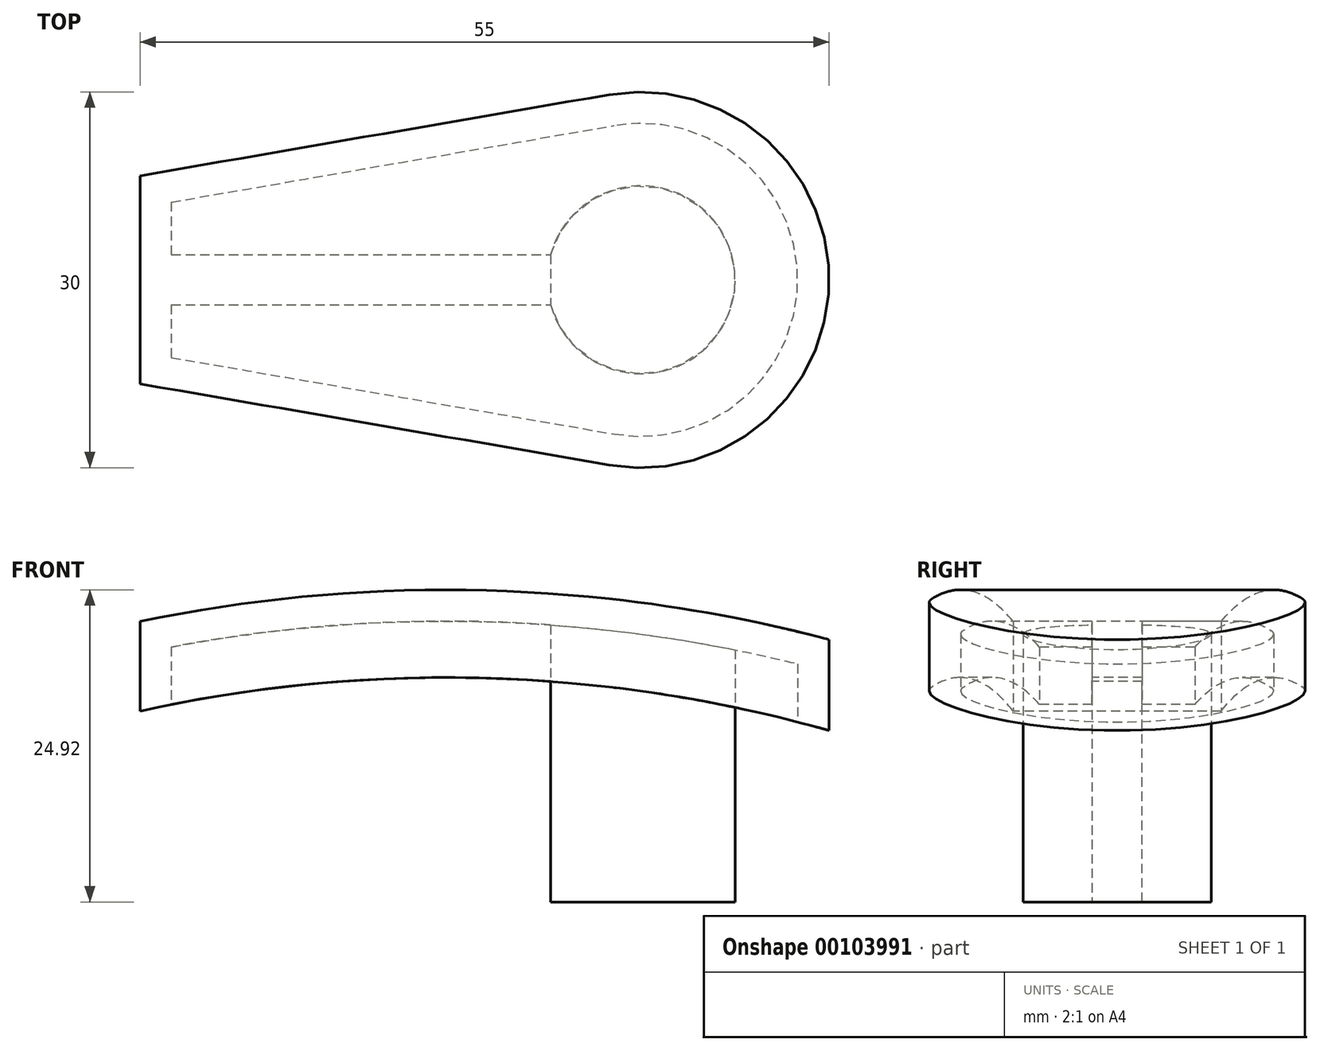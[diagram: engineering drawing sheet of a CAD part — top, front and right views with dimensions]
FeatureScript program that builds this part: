
annotation { "Feature Type Name" : "Feature", "Feature Type Description" : "" }
export const myFeature = defineFeature(function(context is Context, id is Id, definition is map)
    precondition{}
    {
        {
            var Q0;
            Q0=qCreatedBy(makeId("Top.planeOp"),FACE);
            var sketch = newSketch(context, id + "F0", { "sketchPlane" : qUnion([Q0])});
            skArc(sketch, "E0", {"start": v(-2.56, -14.78) * mm, "mid": v(15, 0) * mm, "end": v(-2.56, 14.78) * mm});
            skLineSegment(sketch, "E1", {"start": v(-40, 8.3) * mm, "end": v(-40, 0) * mm});
            skLineSegment(sketch, "E2", {"start": v(-40, 8.3) * mm, "end": v(-2.56, 14.78) * mm});
            skLineSegment(sketch, "E3", {"start": v(0, 0) * mm, "end": v(-66.42, 0) * mm, "construction": true});
            skLineSegment(sketch, "E4.MirrorCS", {"start": v(-40, -8.3) * mm, "end": v(-40, 0) * mm});
            skLineSegment(sketch, "E5.MirrorCS", {"start": v(-40, -8.3) * mm, "end": v(-2.56, -14.78) * mm});
            skSolve(sketch);
        }
        {
            var Q0;
            Q0=makeQuery(id+"F0.imprint","IMPRINT",FACE,{"disambiguationData":[TD([[makeQuery(id+"F0.imprint","IMPRINT",EDGE,{"derivedFrom":sQuery(id+"F0.wireOp",EDGE,"E0")}),1.0]])]});
            extrude(context, id + "F1", {"entities" : qUnion([Q0]), "endBound" : BoundingType.SYMMETRIC, "depth" : 30 * mm});
        }
        {
            var Q0;
            Q0=qCreatedBy(makeId("Front.planeOp"),FACE);
            var sketch = newSketch(context, id + "F2", { "sketchPlane" : qUnion([Q0])});
            skArc(sketch, "E6", {"start": v(44.87, -1.46) * mm, "mid": v(-1.69, 14.1) * mm, "end": v(-50.58, 9.7) * mm});
            skArc(sketch, "E7.0", {"start": v(41.34, -7.5) * mm, "mid": v(-2.5, 7.16) * mm, "end": v(-48.53, 3) * mm});
            skLineSegment(sketch, "E8", {"start": v(-50.58, 9.7) * mm, "end": v(-50.58, 31.79) * mm});
            skLineSegment(sketch, "E9", {"start": v(-50.6, 31.79) * mm, "end": v(44.87, 31.79) * mm});
            skLineSegment(sketch, "E10", {"start": v(44.87, 31.79) * mm, "end": v(44.87, -1.46) * mm});
            skLineSegment(sketch, "E11", {"start": v(-48.53, 3) * mm, "end": v(-48.53, -27.97) * mm});
            skLineSegment(sketch, "E12", {"start": v(-48.53, -27.97) * mm, "end": v(41.34, -29.6) * mm});
            skLineSegment(sketch, "E13", {"start": v(41.34, -29.6) * mm, "end": v(41.34, -7.5) * mm});
            skSolve(sketch);
        }
        {
            var Q0;
            Q0=makeQuery(id+"F2.imprint","IMPRINT",FACE,{"disambiguationData":[TD([[makeQuery(id+"F2.imprint","IMPRINT",EDGE,{"derivedFrom":sQuery(id+"F2.wireOp",EDGE,"E6")}),-1.0]])]});
            var Q1;
            Q1=makeQuery(id+"F2.imprint","IMPRINT",FACE,{"disambiguationData":[TD([[makeQuery(id+"F2.imprint","IMPRINT",EDGE,{"derivedFrom":sQuery(id+"F2.wireOp",EDGE,"E7.0")}),1.0]])]});
            extrude(context, id + "F3", {"entities" : qUnion([Q0, Q1]), "operationType" : NewBodyOperationType.REMOVE, "endBound" : BoundingType.SYMMETRIC, "oppositeDirection" : true, "depth" : 40 * mm});
        }
        {
            var Q0;
            Q0=makeQuery(id+"F3.boolean.opBoolean","COPY",FACE,{"derivedFrom":makeQuery(id+"F3.opExtrude","SWEPT_FACE",FACE,{"disambiguationData":[OSD([sQuery(id+"F2.wireOp",EDGE,"E7.0")])]})});
            shell(context, id + "F4", {"entities" : qUnion([Q0]), "thickness" : 2.5 * mm});
        }
        {
            var Q0;
            Q0=qCreatedBy(makeId("Top.planeOp"),FACE);
            cPlane(context, id + "F5", {"entities" : qUnion([Q0]), "cplaneType" : CPlaneType.OFFSET, "offset" : 10 * mm, "oppositeDirection" : true, "width" : 150 * mm, "height" : 150 * mm});
        }
        {
            var Q0;
            Q0=qCreatedBy(id+"F5.planeOp",FACE);
            var sketch = newSketch(context, id + "F6", { "sketchPlane" : qUnion([Q0])});
            skCircle(sketch, "E14", {"center": v(0, 0) * mm, "radius": 7.5 * mm});
            skSolve(sketch);
        }
        {
            var Q0;
            Q0=makeQuery(id+"F6.imprint","IMPRINT",FACE,{"disambiguationData":[TD([[makeQuery(id+"F6.imprint","IMPRINT",EDGE,{"derivedFrom":sQuery(id+"F6.wireOp",EDGE,"E14")}),1.0]])]});
            extrude(context, id + "F7", {"entities" : qUnion([Q0]), "operationType" : NewBodyOperationType.ADD, "endBound" : BoundingType.UP_TO_NEXT, "depth" : 25 * mm});
        }
        {
            var Q0;
            Q0=qCreatedBy(id+"F5.planeOp",FACE);
            var sketch = newSketch(context, id + "F8", { "sketchPlane" : qUnion([Q0])});
            skLineSegment(sketch, "E15.bottom", {"start": v(-37.5, -2) * mm, "end": v(-3.59, -2) * mm});
            skLineSegment(sketch, "E15.top", {"start": v(-37.5, 2) * mm, "end": v(-3.59, 2) * mm});
            skLineSegment(sketch, "E15.left", {"start": v(-37.5, 2) * mm, "end": v(-37.5, -2) * mm});
            skLineSegment(sketch, "E15.right", {"start": v(-3.59, 2) * mm, "end": v(-3.59, -2) * mm});
            skLineSegment(sketch, "E16", {"start": v(0, 0) * mm, "end": v(15.06, 0) * mm, "construction": true});
            skLineSegment(sketch, "E17.0", {"start": v(-37.5, -6.2) * mm, "end": v(-37.5, 6.2) * mm, "construction": true});
            skSolve(sketch);
        }
        {
            var Q0;
            Q0=makeQuery(id+"F8.imprint","IMPRINT",FACE,{"disambiguationData":[TD([[makeQuery(id+"F8.imprint","IMPRINT",EDGE,{"derivedFrom":sQuery(id+"F8.wireOp",EDGE,"E15.bottom")}),1.0]])]});
            extrude(context, id + "F9", {"entities" : qUnion([Q0]), "operationType" : NewBodyOperationType.ADD, "endBound" : BoundingType.UP_TO_NEXT, "depth" : 25 * mm});
        }
        {
            var Q0;
            Q0=qCreatedBy(makeId("Front.planeOp"),FACE);
            var sketch = newSketch(context, id + "F10", { "sketchPlane" : qUnion([Q0])});
            skArc(sketch, "E18.0", {"start": v(-37.5, 5.77) * mm, "mid": v(-22.43, 7.71) * mm, "end": v(-7.23, 7.6) * mm});
            skLineSegment(sketch, "E19.0", {"start": v(-7.23, 7.6) * mm, "end": v(-7.23, -10) * mm});
            skPoint(sketch, "E20.orphan", {"position": v(-2.56, 7.16) * mm});
            skPoint(sketch, "E21.orphan", {"position": v(-7.23, 12.12) * mm});
            skLineSegment(sketch, "E22.0", {"start": v(-37.5, 5.77) * mm, "end": v(-37.5, -10) * mm});
            skPoint(sketch, "E23.orphan", {"position": v(-40, 5.24) * mm});
            skLineSegment(sketch, "E24", {"start": v(-37.5, -10) * mm, "end": v(-7.23, -10) * mm});
            skSolve(sketch);
        }
        {
            var Q0;
            Q0 = qSketchRegion(id + "F10", true);
            extrude(context, id + "F11", {"entities" : qUnion([Q0]), "operationType" : NewBodyOperationType.REMOVE, "endBound" : BoundingType.SYMMETRIC, "oppositeDirection" : true, "depth" : 25 * mm});
        }
    });
